# Revit family: Pump_Commercial-Sewage_Dewatering-Zoeller-600_3_inch_Vertical_Series
name_source: partatom
category: Mechanical Equipment
revit_build: Autodesk Revit 2014 (Build: 20130308_1515(x64)
units: mm (PartAtom-declared; Revit-internal decimal feet)

## types (29) — shared parameters
Assembly Code = D2010900
Connecter Description = 3"-8 NPT
Cooling = Oil filled
Cord Type = UL listed 3-wire cord
Default Elevation = 0"
Description = Vertical Discharge. Submersible Sewage Or Dewatering Non-Clog Pump for Hazardous Environment
Discharge Diameter = 3"
Discharge Radius = 1 1/2"
Gasket = Buna-N square ring seals
Hardware = Stainless Steel
Height = 29 1/4"
Hertz = 60
Impeller Type (Default) = Ductile Iron Semi-Open
Installation Type = Floor Mounted
Insulation = Class F
Lead Wires Insulation = Class F
Length = 12 5/8"
Lower Bearing = Ball Bearing
Manufacturer = Zoeller
Material = Cast Iron-Zoeller-Powder Coated Epoxy
Max. Water Temp. = 104 °F
Mechanical Seals = Tandem carbon and ceramic
Min. Recommended Fluid Level = 24"
Motor Design Letter = NEMA B
Motor Protection = Thermal sensors with automatic reset
Motor Shaft = Stainless Steel
Operation = Non-Automatic
Price = Prices may vary. Please consult Manufacturer Representative for most up-to-date price list.
Product Documentation Link = http://cdn.qleapahead.com
Product Page URL = http://www.zoellerpumps.com
RPM = 1750
Solid Handling = 2 1/2 Spherical Solids
Tandem Seals = Standard
Type SOW Power Cord Length = 300"
URL = http://www.zoellerpumps.com
Upper Bearing = Ball Bearing
Warranty Information = 18 Months (Limited)
Waste Connection = Yes
Width = 17 9/16"

## per-type parameters (varying)
| type | Amps | Apparent Load | Flow 611-651 @5', 661 @ 10' | Maximum Head | Model | Motor | Phase | Type | Voltage |
| E611 - 230V/1Ph/6.9A/1HP | 7 A | 1587 VA | 250 GPM | 264" | E611 | 1.0 HP | 1 | Capacitor Star/Capacitor Run | 230 V |
| J611 - 200V/3Ph/4.8A/1HP | 5 A | 960 VA | 250 GPM | 264" | J611 | 1.0 HP | 3 | 3 Phase | 200 V |
| F611 - 230V/3Ph/4.2A/3HP | 4 A | 966 VA | 250 GPM | 264" | F611 | 1.0 HP | 3 | 3 Phase | 230 V |
| G611 - 460V/3Ph/2.1A/1HP | 2 A | 966 VA | 250 GPM | 264" | G611 | 1.0 HP | 3 | 3 Phase | 460 V |
| BA611 - 575V/3Ph/1.7A/1HP | 2 A | 978 VA | 250 GPM | 264" | BA611 | 1.0 HP | 3 | 3 Phase | 575 V |
| E621 - 230V/1Ph/8.9A/1.5HP | 9 A | 2047 VA | 320 GPM | 348" | E621 | 1.5 HP | 1 | Capacitor Star/Capacitor Run | 230 V |
| J621 - 200V/3Ph/5.9A/1.5HP | 6 A | 1180 VA | 320 GPM | 348" | J621 | 1.5 HP | 3 | 3 Phase | 200 V |
| F621 - 230V/3Ph/5.1A/1.5HP | 5 A | 1173 VA | 320 GPM | 348" | F621 | 1.5 HP | 3 | 3 Phase | 230 V |
| G621 - 460V/3Ph/2.6A/1.5HP | 3 A | 1196 VA | 320 GPM | 348" | G621 | 1.5 HP | 3 | 3 Phase | 460 V |
| BA621 - 575V/3Ph/2.0A/1.5HP | 2 A | 1150 VA | 320 GPM | 348" | BA621 | 1.5 HP | 3 | 3 Phase | 575 V |
| E631 - 230V/1Ph/14.5A/2HP | 15 A | 3335 VA | 390 GPM | 408" | E631 | 2.0 HP | 1 | Capacitor Star/Capacitor Run | 230 V |
| J631 - 200V/3Ph/7.8A/2HP | 8 A | 1560 VA | 390 GPM | 408" | J631 | 2.0 HP | 3 | 3 Phase | 200 V |
| F631 - 230V/3Ph/6.8A/2HP | 7 A | 1564 VA | 390 GPM | 408" | F631 | 2.0 HP | 3 | 3 Phase | 230 V |
| G631 - 460V/3Ph/3.4A/2HP | 3 A | 1564 VA | 390 GPM | 408" | G631 | 2.0 HP | 3 | 3 Phase | 460 V |
| BA631 - 575V/3Ph/2.7A/2HP | 3 A | 1553 VA | 390 GPM | 408" | BA631 | 2.0 HP | 3 | 3 Phase | 575 V |
| E641 - 230V/1Ph/17.0A/3HP | 17 A | 3910 VA | 420 GPM | 474" (1 Ph), 528" (3 Ph) | E641 | 3.0 HP | 1 | Capacitor Star/Capacitor Run | 230 V |
| J641 - 200V/3Ph/11.0A/3HP | 11 A | 2200 VA | 460 GPM | 474" (1 Ph), 528" (3 Ph) | J641 | 3.0 HP | 3 | 3 Phase | 200 V |
| F641 - 230V/3Ph/9.6A/3HP | 10 A | 2208 VA | 460 GPM | 474" (1 Ph), 528" (3 Ph) | F641 | 3.0 HP | 3 | 3 Phase | 230 V |
| G641 - 460V/3Ph/4.8A/3HP | 5 A | 2208 VA | 460 GPM | 474" (1 Ph), 528" (3 Ph) | G641 | 3.0 HP | 3 | 3 Phase | 460 V |
| BA641 - 575V/3Ph/3.9A/3HP | 4 A | 2243 VA | 460 GPM | 474" (1 Ph), 528" (3 Ph) | BA641 | 3.0 HP | 3 | 3 Phase | 575 V |
| E651 - 230V/1Ph/28.0A/5HP | 28 A | 6440 VA | 475 GPM | 558" (1 Ph), 648" (3 Ph) | E651 | 5.0 HP | 1 | Capacitor Star/Capacitor Run | 230 V |
| J651 - 200V/3Ph/17.5A/5HP | 18 A | 3500 VA | 533 GPM | 558" (1 Ph), 648" (3 Ph) | J651 | 5.0 HP | 3 | 3 Phase | 200 V |
| F651 - 230V/3Ph/15.2A/5HP | 15 A | 3496 VA | 533 GPM | 558" (1 Ph), 648" (3 Ph) | F651 | 5.0 HP | 3 | 3 Phase | 230 V |
| G651 - 460V/3Ph/7.6A/5HP | 8 A | 3496 VA | 533 GPM | 558" (1 Ph), 648" (3 Ph) | G651 | 5.0 HP | 3 | 3 Phase | 460 V |
| BA651 - 575V/3Ph/6.1A/5HP | 6 A | 3508 VA | 533 GPM | 558" (1 Ph), 648" (3 Ph) | BA651 | 5.0 HP | 3 | 3 Phase | 575 V |
| J661 - 200V/3Ph/25.3A/7.5HP | 25 A | 5060 VA | 600 GPM | 780" | J661 | 7.5 HP | 3 | 3 Phase | 200 V |
| F661 - 230V/3Ph/22.0A/7.5HP | 22 A | 5060 VA | 600 GPM | 780" | F661 | 7.5 HP | 3 | 3 Phase | 230 V |
| G661 - 460V/3Ph/11.0A/7.5HP | 11 A | 5060 VA | 600 GPM | 780" | G661 | 7.5 HP | 3 | 3 Phase | 460 V |
| BA661 - 575V/3Ph/9.0A/7.5HP | 9 A | 5175 VA | 600 GPM | 780" | BA661 | 7.5 HP | 3 | 3 Phase | 575 V |

## geometry (parser evidence)
native form markers: Blend x2, Sweep x3
no freeform markers — native parametric forms only
